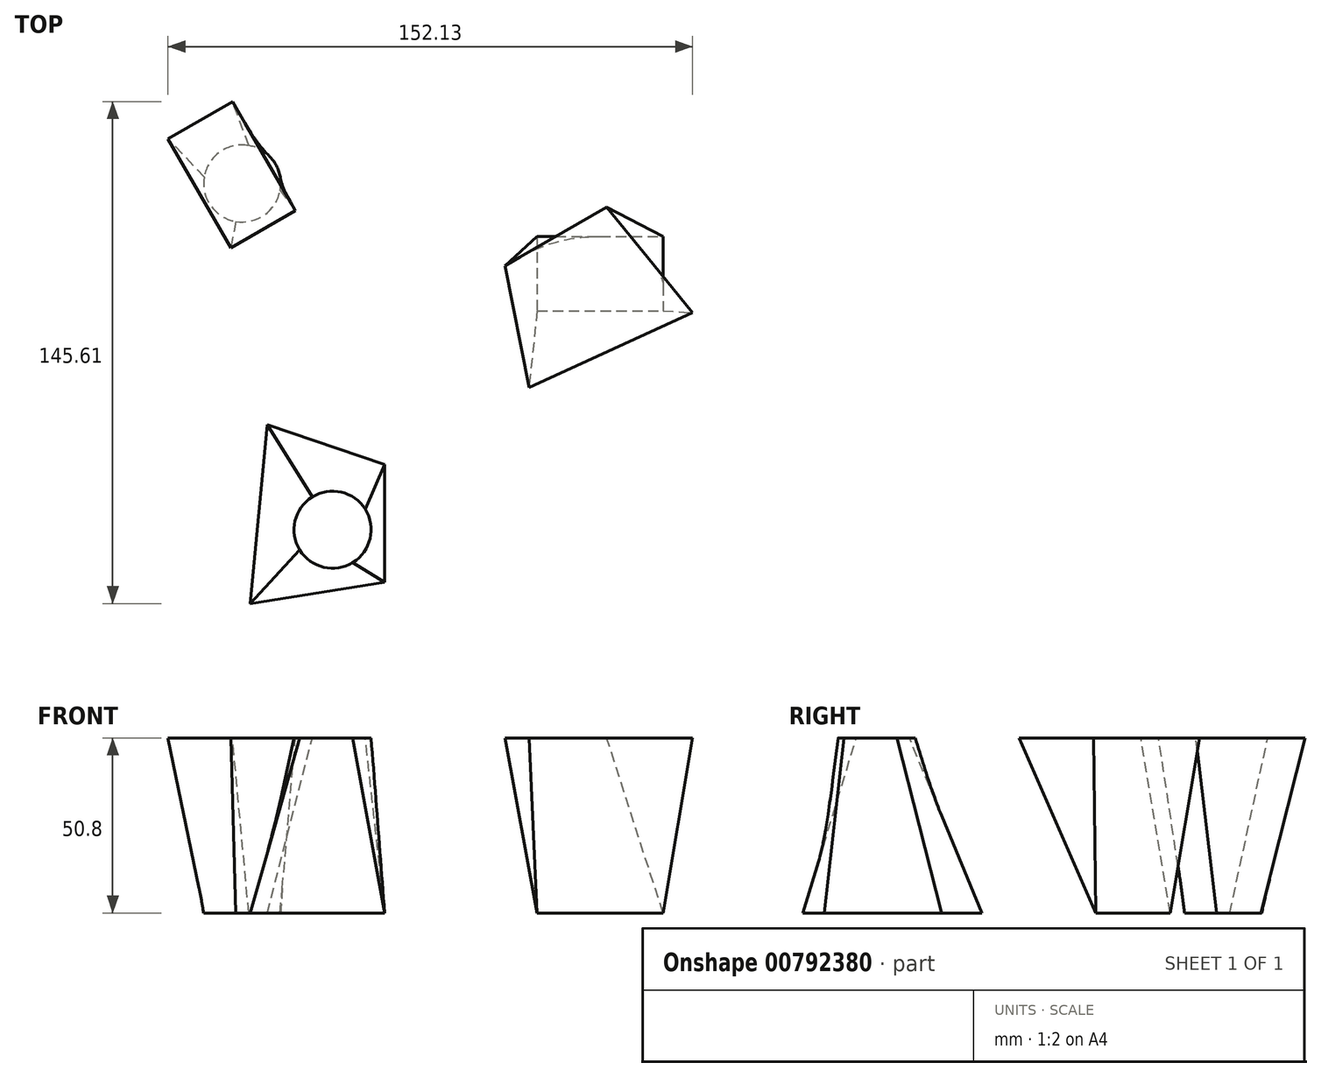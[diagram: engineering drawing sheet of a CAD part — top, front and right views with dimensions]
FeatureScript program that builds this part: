
annotation { "Feature Type Name" : "Feature", "Feature Type Description" : "" }
export const myFeature = defineFeature(function(context is Context, id is Id, definition is map)
    precondition{}
    {
        {
            var Q0;
            Q0=qCreatedBy(makeId("Top.planeOp"),FACE);
            var sketch = newSketch(context, id + "F0", { "sketchPlane" : qUnion([Q0])});
            skCircle(sketch, "E0", {"center": v(-62.28, 52.52) * mm, "radius": 11.18 * mm});
            skLineSegment(sketch, "E1.bottom", {"start": v(23.25, 37.16) * mm, "end": v(59.79, 37.16) * mm});
            skLineSegment(sketch, "E1.top", {"start": v(23.25, 15.57) * mm, "end": v(59.79, 15.57) * mm});
            skLineSegment(sketch, "E1.left", {"start": v(23.25, 37.16) * mm, "end": v(23.25, 15.57) * mm});
            skLineSegment(sketch, "E1.right", {"start": v(59.79, 37.16) * mm, "end": v(59.79, 15.57) * mm});
            skLineSegment(sketch, "E2", {"start": v(-55, -17.45) * mm, "end": v(-20.95, -29.08) * mm});
            skLineSegment(sketch, "E3", {"start": v(-20.95, -29.08) * mm, "end": v(-20.95, -63.13) * mm});
            skLineSegment(sketch, "E4", {"start": v(-20.95, -63.13) * mm, "end": v(-59.98, -69.35) * mm});
            skLineSegment(sketch, "E5", {"start": v(-59.98, -69.35) * mm, "end": v(-55, -17.45) * mm});
            skLineSegment(sketch, "E6", {"start": v(-82.91, 71.7) * mm, "end": v(-82.91, 30.26) * mm, "construction": true});
            skSolve(sketch);
        }
        {
            var Q0;
            Q0=qCreatedBy(makeId("Top.planeOp"),FACE);
            cPlane(context, id + "F1", {"entities" : qUnion([Q0]), "cplaneType" : CPlaneType.OFFSET, "offset" : 50.8 * mm, "width" : 152.4 * mm, "height" : 152.4 * mm});
        }
        {
            var Q0;
            Q0=qCreatedBy(id+"F1.planeOp",FACE);
            var sketch = newSketch(context, id + "F2", { "sketchPlane" : qUnion([Q0])});
            skCircle(sketch, "E7.0", {"center": v(-36.07, -47.94) * mm, "radius": 11.18 * mm});
            skLineSegment(sketch, "E7.1.0", {"start": v(-65.53, 33.82) * mm, "end": v(-46.83, 44.61) * mm});
            skLineSegment(sketch, "E7.1.1", {"start": v(-46.83, 44.61) * mm, "end": v(-65.1, 76.26) * mm});
            skLineSegment(sketch, "E7.1.2", {"start": v(-65.1, 76.26) * mm, "end": v(-83.8, 65.46) * mm});
            skLineSegment(sketch, "E7.1.3", {"start": v(-83.8, 65.46) * mm, "end": v(-65.53, 33.82) * mm});
            skLineSegment(sketch, "E7.2.0", {"start": v(20.9, -6.64) * mm, "end": v(68.33, 15) * mm});
            skLineSegment(sketch, "E7.2.1", {"start": v(68.33, 15) * mm, "end": v(43.42, 45.68) * mm});
            skLineSegment(sketch, "E7.2.2", {"start": v(43.42, 45.68) * mm, "end": v(13.94, 28.66) * mm});
            skLineSegment(sketch, "E7.2.3", {"start": v(13.94, 28.66) * mm, "end": v(20.9, -6.64) * mm});
            skSolve(sketch);
        }
        {
            var Q0;
            Q0=makeQuery(id+"F0.imprint","IMPRINT",FACE,{"disambiguationData":[TD([[makeQuery(id+"F0.imprint","IMPRINT",EDGE,{"derivedFrom":sQuery(id+"F0.wireOp",EDGE,"E0")}),1.0]])]});
            var Q1;
            Q1=makeQuery(id+"F2.imprint","IMPRINT",FACE,{"disambiguationData":[TD([[makeQuery(id+"F2.imprint","IMPRINT",EDGE,{"derivedFrom":sQuery(id+"F2.wireOp",EDGE,"E7.1.0")}),1.0]])]});
            loft(context, id + "F3", {"sheetProfilesArray" : [{ "sheetProfileEntities" : qUnion([Q0]) }, { "sheetProfileEntities" : qUnion([Q1]) }]});
        }
        {
            var Q0;
            Q0=makeQuery(id+"F0.imprint","IMPRINT",FACE,{"disambiguationData":[TD([[makeQuery(id+"F0.imprint","IMPRINT",EDGE,{"derivedFrom":sQuery(id+"F0.wireOp",EDGE,"E2")}),-1.0]])]});
            var Q1;
            Q1=makeQuery(id+"F2.imprint","IMPRINT",FACE,{"disambiguationData":[TD([[makeQuery(id+"F2.imprint","IMPRINT",EDGE,{"derivedFrom":sQuery(id+"F2.wireOp",EDGE,"E7.0")}),1.0]])]});
            loft(context, id + "F4", {"sheetProfilesArray" : [{ "sheetProfileEntities" : qUnion([Q0]) }, { "sheetProfileEntities" : qUnion([Q1]) }]});
        }
        {
            var Q0;
            Q0=makeQuery(id+"F0.imprint","IMPRINT",FACE,{"disambiguationData":[TD([[makeQuery(id+"F0.imprint","IMPRINT",EDGE,{"derivedFrom":sQuery(id+"F0.wireOp",EDGE,"E1.bottom")}),-1.0]])]});
            var Q1;
            Q1=makeQuery(id+"F2.imprint","IMPRINT",FACE,{"disambiguationData":[TD([[makeQuery(id+"F2.imprint","IMPRINT",EDGE,{"derivedFrom":sQuery(id+"F2.wireOp",EDGE,"E7.2.0")}),1.0]])]});
            loft(context, id + "F5", {"sheetProfilesArray" : [{ "sheetProfileEntities" : qUnion([Q0]) }, { "sheetProfileEntities" : qUnion([Q1]) }]});
        }
    });
